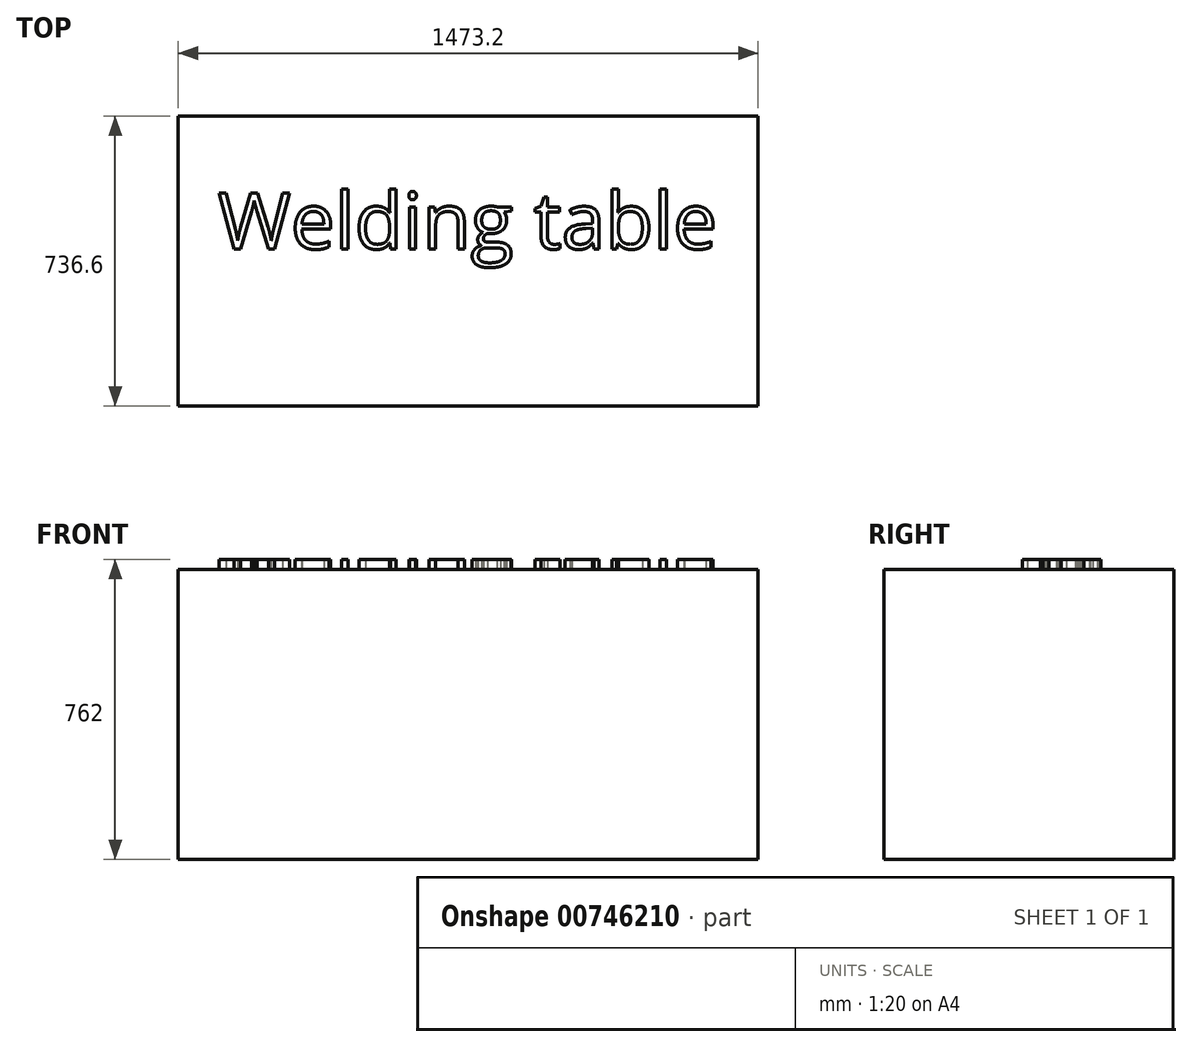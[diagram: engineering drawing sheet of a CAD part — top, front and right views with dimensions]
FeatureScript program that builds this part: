
annotation { "Feature Type Name" : "Feature", "Feature Type Description" : "" }
export const myFeature = defineFeature(function(context is Context, id is Id, definition is map)
    precondition{}
    {
        {
            var Q0;
            Q0=qCreatedBy(makeId("Top.planeOp"),FACE);
            var sketch = newSketch(context, id + "F0", { "sketchPlane" : qUnion([Q0])});
            skLineSegment(sketch, "E0.bottom", {"start": v(736.6, -368.3) * mm, "end": v(-736.6, -368.3) * mm});
            skLineSegment(sketch, "E0.top", {"start": v(736.6, 368.3) * mm, "end": v(-736.6, 368.3) * mm});
            skLineSegment(sketch, "E0.left", {"start": v(736.6, -368.3) * mm, "end": v(736.6, 368.3) * mm});
            skLineSegment(sketch, "E0.right", {"start": v(-736.6, -368.3) * mm, "end": v(-736.6, 368.3) * mm});
            skPoint(sketch, "E0.middle", {"position": v(0, 0) * mm});
            skSolve(sketch);
        }
        {
            var Q0;
            Q0 = qSketchRegion(id + "F0", true);
            extrude(context, id + "F1", {"entities" : qUnion([Q0]), "depth" : 736.6 * mm, "offsetDistance" : 25.4 * mm});
        }
        {
            var Q0;
            Q0=makeQuery(id+"F1.opExtrude","CAP_FACE",FACE,{"disambiguationData":[OSD([sQuery(id+"F0.wireOp",EDGE,"E0.bottom"),sQuery(id+"F0.wireOp",EDGE,"E0.top"),sQuery(id+"F0.wireOp",EDGE,"E0.left"),sQuery(id+"F0.wireOp",EDGE,"E0.right")])],"isStart":false});
            var sketch = newSketch(context, id + "F2", { "sketchPlane" : qUnion([Q0])});
            skText(sketch, "E1", { "text": "Welding table", "fontName": "OpenSans-Regular.ttf"});
            const initialGuessF2  = {"E1": [-0.635, 0.03094, 1, 0, 0.14342]};
            skSetInitialGuess(sketch, initialGuessF2);
            skSolve(sketch);
        }
        {
            var Q0;
            Q0 = qSketchRegion(id + "F2", true);
            extrude(context, id + "F3", {"entities" : qUnion([Q0]), "operationType" : NewBodyOperationType.ADD, "depth" : 25.4 * mm, "offsetDistance" : 25.4 * mm});
        }
    });
